# Revit family: EnOcean Gateway _434
name_source: partatom
category: Electrical Fixtures
revit_build: Autodesk Revit 2018 (Build: 20170223_1515(x64)
units: mm (PartAtom-declared; Revit-internal decimal feet)

## family parameters
Always vertical = No
Cut with Voids When Loaded = No
Maintain Annotation Orientation = No
Part Type = Normal
Room Calculation Point = No
Round Connector Dimension = Use Diameter
Shared = No
Work Plane-Based = Yes

## types (1)
- ENOCEAN GATEWAY (868 MHz)
    ARIB = STD-T108 (434/2)
    Ambient temperature = 0 °C to +50 °C
    Cable rating = All cables must be mains rated.
    Colour = White: RAL 9002
    DALI : = Removable 2-part connector block Wire size: 0.5 mm² – 2.5 mm² solid or stranded
    DALI consumption = 20 mA
    DALI supply input = 13 V – 22.5 V
    Default Elevation = 1219 mm
    Dimensions: = 110 mm (⌀) × 58 mm
    EMC = EN 55015 EN 61547
    Environment: = Complies with WEEE and RoHS directives.
    IP code: = IP30
    Manufacturer = helvar
    Max. No. of switch units per gateway = 20
    Model = 434
    Operating frequency = model:434 Frequency:868MHz
    RED = EN 300220-2 (434) EN 301489-3 (434)
    Range (switches) = : Typical EnOcean Switches: 30 m (unobstructed space
    Relative humidity = Max. 90 %, noncondensing
    Safety = EN 60950-1
    Storage temperature = –10 °C to +70 °C
    Supported profile = EnOcean EEP F6–02–xx, F6-04–xx
 (PTM 210/215 normal mode)
    Weight = 75 g
    Wireless protocol = ISO/IEC 14543-3-10

## geometry (parser evidence)
native form markers: Sweep x6
no freeform markers — native parametric forms only
